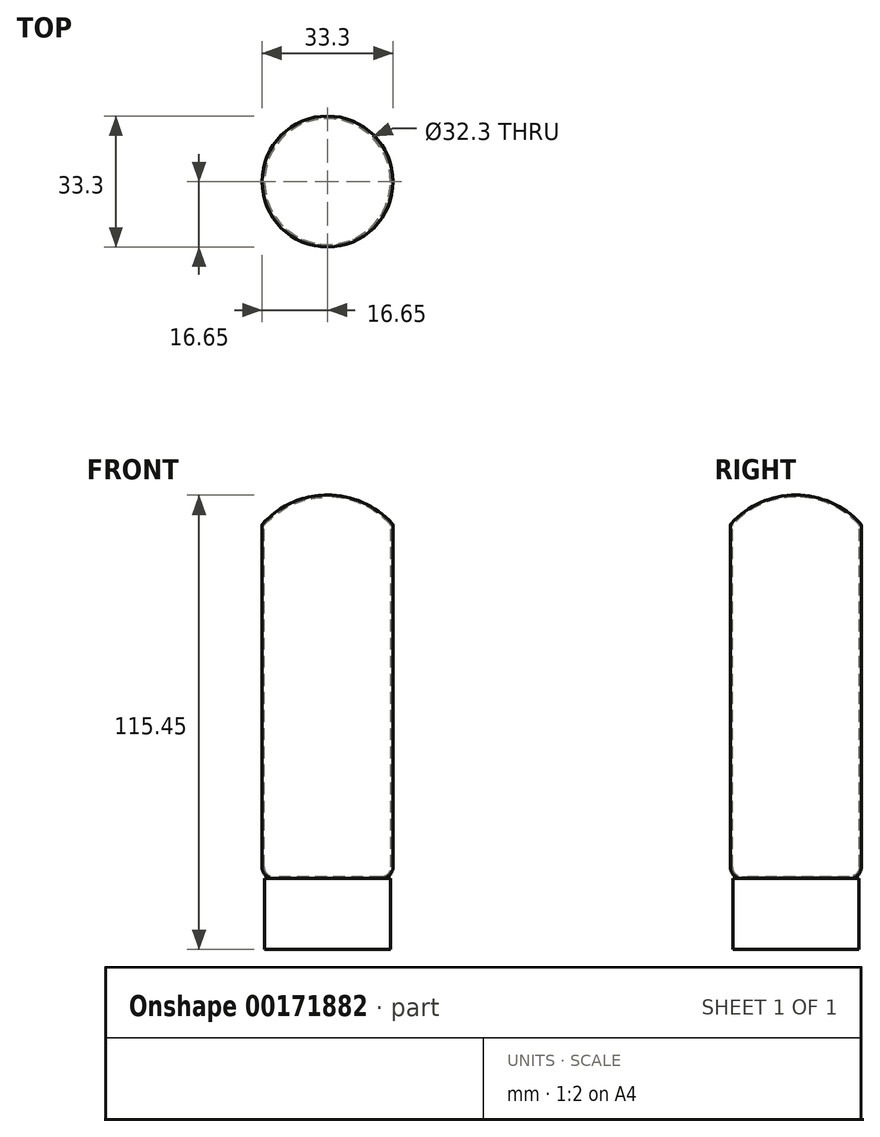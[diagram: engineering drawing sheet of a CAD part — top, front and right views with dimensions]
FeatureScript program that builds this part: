
annotation { "Feature Type Name" : "Feature", "Feature Type Description" : "" }
export const myFeature = defineFeature(function(context is Context, id is Id, definition is map)
    precondition{}
    {
        {
            var Q0;
            Q0=qCreatedBy(makeId("Front.planeOp"),FACE);
            var sketch = newSketch(context, id + "F0", { "sketchPlane" : qUnion([Q0])});
            skLineSegment(sketch, "E0", {"start": v(0, 0) * mm, "end": v(-16, 0) * mm});
            skLineSegment(sketch, "E1", {"start": v(-16, 0) * mm, "end": v(-16, 18) * mm});
            skLineSegment(sketch, "E2", {"start": v(-13.65, 18) * mm, "end": v(0, 18) * mm});
            skLineSegment(sketch, "E3", {"start": v(0, 33.7) * mm, "end": v(0, -19.5) * mm, "construction": true});
            skLineSegment(sketch, "E4", {"start": v(-16.65, 21) * mm, "end": v(-16.65, 107.58) * mm});
            skPoint(sketch, "E5.visualSharp", {"position": v(-16, 18) * mm});
            skArc(sketch, "E5.filletArc", {"start": v(-16.65, 21) * mm, "mid": v(-15.77, 18.88) * mm, "end": v(-13.65, 18) * mm});
            skLineSegment(sketch, "E6", {"start": v(-16, 18) * mm, "end": v(-13.65, 18) * mm});
            skArc(sketch, "E7", {"start": v(0, 115.45) * mm, "mid": v(-8.95, 113.57) * mm, "end": v(-16.39, 108.25) * mm});
            skPoint(sketch, "E8.end.orphan", {"position": v(0, 107.62) * mm});
            skPoint(sketch, "E9.visualSharp", {"position": v(-16.65, 107.96) * mm});
            skArc(sketch, "E9.filletArc", {"start": v(-16.39, 108.25) * mm, "mid": v(-16.58, 107.94) * mm, "end": v(-16.65, 107.58) * mm});
            skLineSegment(sketch, "E10", {"start": v(0, 55.36) * mm, "end": v(0, 175.54) * mm, "construction": true});
            skLineSegment(sketch, "E11", {"start": v(0, 115.45) * mm, "end": v(0, 0) * mm});
            skSolve(sketch);
        }
        {
            var Q0;
            {var subQ2=sQuery(id+"F0.wireOp",EDGE,"E0");Q0=makeQuery(id+"F0.imprint","IMPRINT",FACE,{"disambiguationData":[TD([[makeQuery(id+"F0.imprint","IMPRINT",EDGE,{"derivedFrom":subQ2}),-1.0]])]});}
            var Q1;
            Q1=sQuery(id+"F0.wireOp",EDGE,"E11");
            revolve(context, id + "F1", {"entities" : qUnion([Q0]), "axis" : qUnion([Q1]), "revolveType" : RevolveType.FULL});
        }
        {
            var Q0;
            {var subQ1=sQuery(id+"F0.wireOp",EDGE,"E2");Q0=makeQuery(id+"F0.imprint","IMPRINT",FACE,{"disambiguationData":[TD([[makeQuery(id+"F0.imprint","IMPRINT",EDGE,{"derivedFrom":subQ1}),1.0]])]});}
            var Q1;
            Q1=sQuery(id+"F0.wireOp",EDGE,"E11");
            revolve(context, id + "F2", {"entities" : qUnion([Q0]), "axis" : qUnion([Q1]), "revolveType" : RevolveType.FULL});
        }
        {
            var Q0;
            Q0=makeQuery(id+"F2.opRevolve","SWEPT_FACE",FACE,{"disambiguationData":[OSD([sQuery(id+"F0.wireOp",EDGE,"E4")])]});
            var Q1;
            Q1=makeQuery(id+"F2.opRevolve","SWEPT_FACE",FACE,{"disambiguationData":[OSD([sQuery(id+"F0.wireOp",EDGE,"E7")])]});
            var Q2;
            Q2=makeQuery(id+"F2.opRevolve","SWEPT_BODY",BODY,{"disambiguationData":[OSD([sQuery(id+"F0.wireOp",EDGE,"E2"),sQuery(id+"F0.wireOp",EDGE,"E4"),sQuery(id+"F0.wireOp",EDGE,"E5.filletArc"),sQuery(id+"F0.wireOp",EDGE,"E7"),sQuery(id+"F0.wireOp",EDGE,"E9.filletArc"),sQuery(id+"F0.wireOp",EDGE,"E11")])]});
            shell(context, id + "F3", {"isHollow" : true, "entities" : qUnion([Q0, Q1]), "parts" : qUnion([Q2]), "thickness" : 0.5 * mm});
        }
    });
